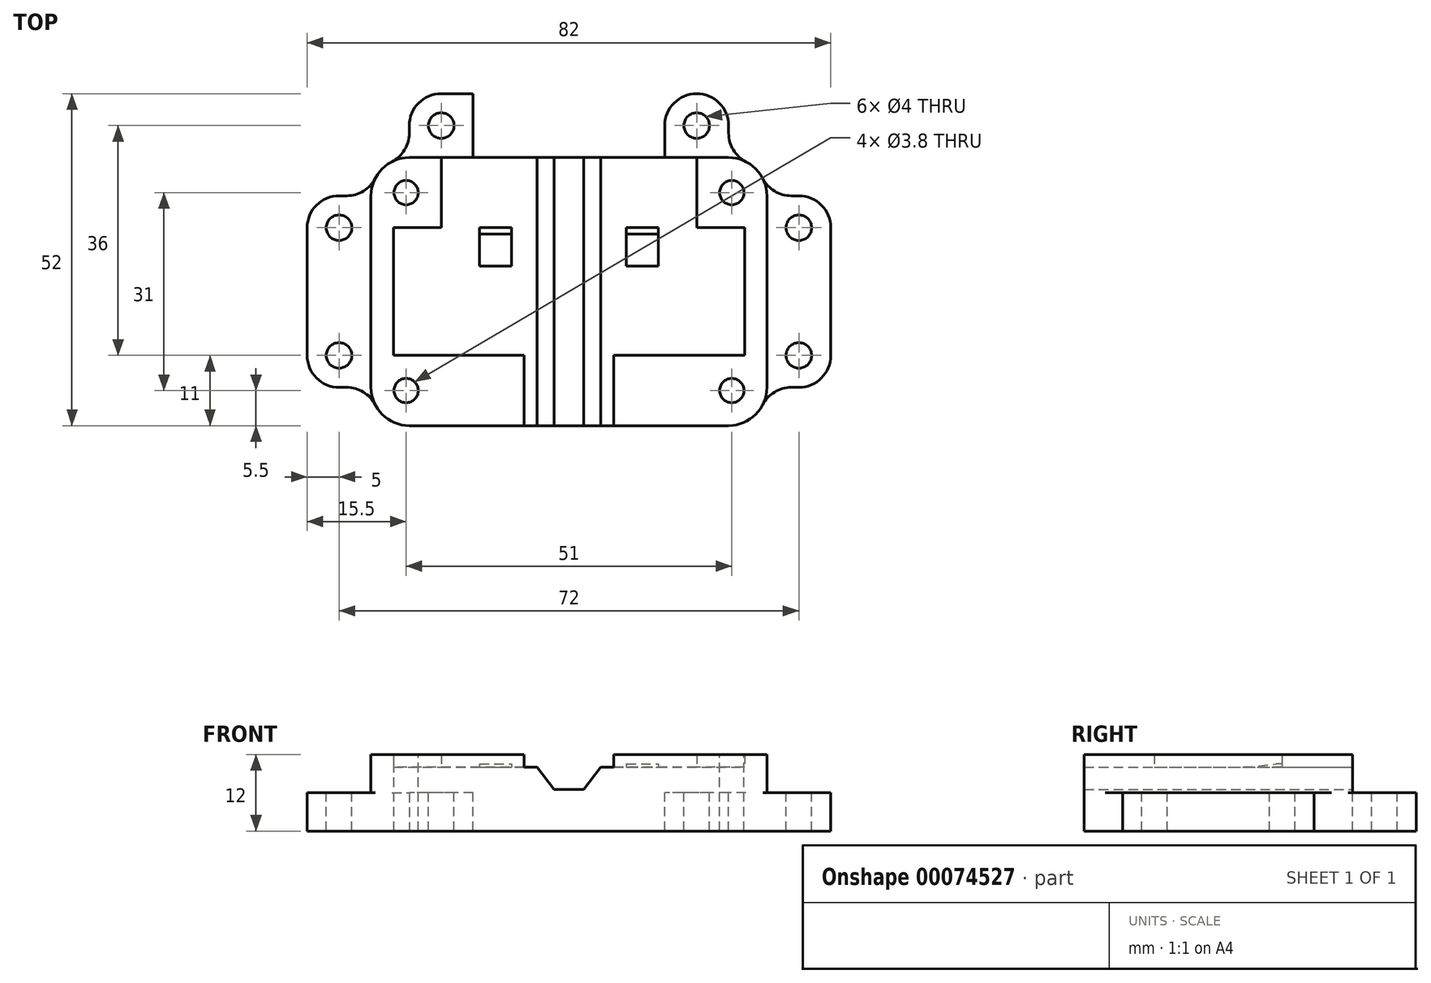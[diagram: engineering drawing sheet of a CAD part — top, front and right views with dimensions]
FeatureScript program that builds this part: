
annotation { "Feature Type Name" : "Feature", "Feature Type Description" : "" }
export const myFeature = defineFeature(function(context is Context, id is Id, definition is map)
    precondition{}
    {
        {
            var Q0;
            Q0=qCreatedBy(makeId("Front.planeOp"),FACE);
            var sketch = newSketch(context, id + "F0", { "sketchPlane" : qUnion([Q0])});
            skLineSegment(sketch, "E0.bottom", {"start": v(0, 0) * mm, "end": v(62, 0) * mm});
            skLineSegment(sketch, "E0.top", {"start": v(0, 10) * mm, "end": v(62, 10) * mm, "construction": true});
            skLineSegment(sketch, "E0.left", {"start": v(0, 0) * mm, "end": v(0, 10) * mm});
            skLineSegment(sketch, "E0.right", {"start": v(62, 0) * mm, "end": v(62, 10) * mm});
            skLineSegment(sketch, "E1", {"start": v(0, 10) * mm, "end": v(26, 10) * mm});
            skLineSegment(sketch, "E2", {"start": v(62, 10) * mm, "end": v(36, 10) * mm});
            skLineSegment(sketch, "E3", {"start": v(26, 10) * mm, "end": v(28.7, 6.5) * mm});
            skLineSegment(sketch, "E4", {"start": v(28.7, 6.5) * mm, "end": v(33.3, 6.5) * mm});
            skLineSegment(sketch, "E5", {"start": v(36, 10) * mm, "end": v(33.3, 6.5) * mm});
            skSolve(sketch);
        }
        {
            var Q0;
            Q0 = qSketchRegion(id + "F0", true);
            extrude(context, id + "F1", {"entities" : qUnion([Q0]), "depth" : 42 * mm});
        }
        {
            var Q0;
            Q0=makeQuery(id+"F1.opExtrude","SWEPT_FACE",FACE,{"disambiguationData":[OSD([sQuery(id+"F0.wireOp",EDGE,"E1")])]});
            var sketch = newSketch(context, id + "F2", { "sketchPlane" : qUnion([Q0])});
            skLineSegment(sketch, "E6", {"start": v(17, -8) * mm, "end": v(45, -8) * mm});
            skLineSegment(sketch, "E7", {"start": v(45, -8) * mm, "end": v(56.5, -27) * mm});
            skLineSegment(sketch, "E8", {"start": v(56.5, -27) * mm, "end": v(5.5, -27) * mm});
            skLineSegment(sketch, "E9", {"start": v(5.5, -27) * mm, "end": v(17, -8) * mm});
            skLineSegment(sketch, "E10.0", {"start": v(28.7, 0) * mm, "end": v(33.3, 0) * mm, "construction": true});
            skLineSegment(sketch, "E11", {"start": v(31, 0) * mm, "end": v(31, -8) * mm, "construction": true});
            skLineSegment(sketch, "E12", {"start": v(31, -8) * mm, "end": v(31, -27) * mm, "construction": true});
            skSolve(sketch);
        }
        {
            var Q0;
            {var subQ1=sQuery(id+"F2.wireOp",EDGE,"E9");Q0=makeQuery(id+"F2.imprint","IMPRINT",FACE,{"disambiguationData":[TD([[makeQuery(id+"F2.imprint","IMPRINT",EDGE,{"derivedFrom":subQ1}),1.0]])]});}
            var sketch = newSketch(context, id + "F3", { "sketchPlane" : qUnion([Q0])});
            skLineSegment(sketch, "E13.0", {"start": v(0, -42) * mm, "end": v(26, -42) * mm, "construction": true});
            skLineSegment(sketch, "E14.0", {"start": v(62, -42) * mm, "end": v(36, -42) * mm, "construction": true});
            skLineSegment(sketch, "E15", {"start": v(24, -42) * mm, "end": v(24, -31) * mm});
            skLineSegment(sketch, "E16", {"start": v(0, -42) * mm, "end": v(24, -42) * mm});
            skLineSegment(sketch, "E17", {"start": v(62, -42) * mm, "end": v(38, -42) * mm});
            skLineSegment(sketch, "E18", {"start": v(38, -42) * mm, "end": v(38, -31) * mm});
            skLineSegment(sketch, "E19", {"start": v(24, -31) * mm, "end": v(3.5, -31) * mm});
            skLineSegment(sketch, "E20", {"start": v(3.5, -31) * mm, "end": v(3.5, -11) * mm});
            skLineSegment(sketch, "E21", {"start": v(0, 0) * mm, "end": v(0, -42) * mm});
            skLineSegment(sketch, "E22", {"start": v(38, -31) * mm, "end": v(58.5, -31) * mm});
            skLineSegment(sketch, "E23", {"start": v(58.5, -31) * mm, "end": v(58.5, -11) * mm});
            skLineSegment(sketch, "E24", {"start": v(62, 0) * mm, "end": v(62, -42) * mm});
            skLineSegment(sketch, "E25", {"start": v(3.5, -11) * mm, "end": v(11, -11) * mm});
            skLineSegment(sketch, "E26", {"start": v(11, -11) * mm, "end": v(11, 0) * mm});
            skLineSegment(sketch, "E27", {"start": v(11, 0) * mm, "end": v(0, 0) * mm});
            skLineSegment(sketch, "E28", {"start": v(58.5, -11) * mm, "end": v(51, -11) * mm});
            skLineSegment(sketch, "E29", {"start": v(51, -11) * mm, "end": v(51, 0) * mm});
            skLineSegment(sketch, "E30", {"start": v(51, 0) * mm, "end": v(62, 0) * mm});
            skSolve(sketch);
        }
        {
            var Q0;
            Q0 = qSketchRegion(id + "F3", true);
            extrude(context, id + "F4", {"entities" : qUnion([Q0]), "operationType" : NewBodyOperationType.ADD, "depth" : 2 * mm});
        }
        {
            var Q0;
            Q0=makeQuery(id+"F4.opExtrude","CAP_FACE",FACE,{"disambiguationData":[OSD([sQuery(id+"F3.wireOp",EDGE,"E15"),sQuery(id+"F3.wireOp",EDGE,"E16"),sQuery(id+"F3.wireOp",EDGE,"E19"),sQuery(id+"F3.wireOp",EDGE,"E20"),sQuery(id+"F3.wireOp",EDGE,"E21"),sQuery(id+"F3.wireOp",EDGE,"E25"),sQuery(id+"F3.wireOp",EDGE,"E26"),sQuery(id+"F3.wireOp",EDGE,"E27")])],"isStart":false});
            var sketch = newSketch(context, id + "F5", { "sketchPlane" : qUnion([Q0])});
            skLineSegment(sketch, "E31.0", {"start": v(0, -42) * mm, "end": v(0, 0) * mm, "construction": true});
            skLineSegment(sketch, "E31.1", {"start": v(62, 0) * mm, "end": v(62, -42) * mm, "construction": true});
            skLineSegment(sketch, "E31.2", {"start": v(0, -42) * mm, "end": v(62, -42) * mm, "construction": true});
            skLineSegment(sketch, "E31.3", {"start": v(0, 0) * mm, "end": v(62, 0) * mm, "construction": true});
            skLineSegment(sketch, "E32", {"start": v(0, -36.5) * mm, "end": v(62, -36.5) * mm, "construction": true});
            skLineSegment(sketch, "E33", {"start": v(0, -5.5) * mm, "end": v(62, -5.5) * mm, "construction": true});
            skLineSegment(sketch, "E34", {"start": v(5.5, 0) * mm, "end": v(5.5, -42) * mm, "construction": true});
            skLineSegment(sketch, "E35", {"start": v(56.5, 0) * mm, "end": v(56.5, -42) * mm, "construction": true});
            skCircle(sketch, "E36", {"center": v(5.5, -5.5) * mm, "radius": 1.9 * mm});
            skCircle(sketch, "E37", {"center": v(56.5, -5.5) * mm, "radius": 1.9 * mm});
            skCircle(sketch, "E38", {"center": v(5.5, -36.5) * mm, "radius": 1.9 * mm});
            skCircle(sketch, "E39", {"center": v(56.5, -36.5) * mm, "radius": 1.9 * mm});
            skSolve(sketch);
        }
        {
            var Q0;
            Q0 = qSketchRegion(id + "F5", true);
            var Q1;
            Q1=makeQuery(id+"F1.opExtrude","SWEPT_FACE",FACE,{"disambiguationData":[OSD([sQuery(id+"F0.wireOp",EDGE,"E0.bottom")])]});
            extrude(context, id + "F6", {"entities" : qUnion([Q0]), "operationType" : NewBodyOperationType.REMOVE, "endBound" : BoundingType.UP_TO_SURFACE, "oppositeDirection" : true, "endBoundEntityFace" : qUnion([Q1]), "depth" : 25 * mm});
        }
        {
            var Q0;
            Q0=makeQuery(id+"F4.boolean.opBoolean","MERGE",EDGE,{"derivedFrom":[makeQuery(id+"F1.opExtrude","CAP_EDGE",EDGE,{"disambiguationData":[OSD([sQuery(id+"F0.wireOp",EDGE,"E0.left")])],"isStart":false}),makeQuery(id+"F4.opExtrude","SWEPT_EDGE",EDGE,{"disambiguationData":[OSD([sQuery(id+"F3.wireOp",EDGE,"E16"),sQuery(id+"F3.wireOp",EDGE,"E21")])]})]});
            var Q1;
            Q1=makeQuery(id+"F4.boolean.opBoolean","MERGE",EDGE,{"derivedFrom":[makeQuery(id+"F1.opExtrude","CAP_EDGE",EDGE,{"disambiguationData":[OSD([sQuery(id+"F0.wireOp",EDGE,"E0.left")])],"isStart":true}),makeQuery(id+"F4.opExtrude","SWEPT_EDGE",EDGE,{"disambiguationData":[OSD([sQuery(id+"F3.wireOp",EDGE,"E21"),sQuery(id+"F3.wireOp",EDGE,"E27")])]})]});
            var Q2;
            Q2=makeQuery(id+"F4.boolean.opBoolean","MERGE",EDGE,{"derivedFrom":[makeQuery(id+"F1.opExtrude","CAP_EDGE",EDGE,{"disambiguationData":[OSD([sQuery(id+"F0.wireOp",EDGE,"E0.right")])],"isStart":false}),makeQuery(id+"F4.opExtrude","SWEPT_EDGE",EDGE,{"disambiguationData":[OSD([sQuery(id+"F3.wireOp",EDGE,"E17"),sQuery(id+"F3.wireOp",EDGE,"E24")])]})]});
            var Q3;
            Q3=makeQuery(id+"F4.boolean.opBoolean","MERGE",EDGE,{"derivedFrom":[makeQuery(id+"F1.opExtrude","CAP_EDGE",EDGE,{"disambiguationData":[OSD([sQuery(id+"F0.wireOp",EDGE,"E0.right")])],"isStart":true}),makeQuery(id+"F4.opExtrude","SWEPT_EDGE",EDGE,{"disambiguationData":[OSD([sQuery(id+"F3.wireOp",EDGE,"E24"),sQuery(id+"F3.wireOp",EDGE,"E30")])]})]});
            fillet(context, id + "F7", {"entities" : qUnion([Q0, Q1, Q2, Q3]), "radius" : 6 * mm, "tangentPropagation" : true, "allowEdgeOverflow" : false});
        }
        {
            var Q0;
            Q0=makeQuery(id+"F4.boolean.opBoolean","MERGE",FACE,{"derivedFrom":[makeQuery(id+"F1.opExtrude","SWEPT_FACE",FACE,{"disambiguationData":[OSD([sQuery(id+"F0.wireOp",EDGE,"E0.right")])]}),makeQuery(id+"F4.opExtrude","SWEPT_FACE",FACE,{"disambiguationData":[OSD([sQuery(id+"F3.wireOp",EDGE,"E24")])]})]});
            var sketch = newSketch(context, id + "F8", { "sketchPlane" : qUnion([Q0])});
            skLineSegment(sketch, "E40.bottom", {"start": v(-6, 0) * mm, "end": v(-36, 0) * mm});
            skLineSegment(sketch, "E40.top", {"start": v(-6, 6) * mm, "end": v(-36, 6) * mm});
            skLineSegment(sketch, "E40.left", {"start": v(-6, 0) * mm, "end": v(-6, 6) * mm});
            skLineSegment(sketch, "E40.right", {"start": v(-36, 0) * mm, "end": v(-36, 6) * mm});
            skSolve(sketch);
        }
        {
            var Q0;
            Q0 = qSketchRegion(id + "F8", true);
            extrude(context, id + "F9", {"entities" : qUnion([Q0]), "operationType" : NewBodyOperationType.ADD, "depth" : 10 * mm});
        }
        {
            var Q0;
            Q0=makeQuery(id+"F4.boolean.opBoolean","MERGE",FACE,{"derivedFrom":[makeQuery(id+"F1.opExtrude","SWEPT_FACE",FACE,{"disambiguationData":[OSD([sQuery(id+"F0.wireOp",EDGE,"E0.left")])]}),makeQuery(id+"F4.opExtrude","SWEPT_FACE",FACE,{"disambiguationData":[OSD([sQuery(id+"F3.wireOp",EDGE,"E21")])]})]});
            var sketch = newSketch(context, id + "F10", { "sketchPlane" : qUnion([Q0])});
            skLineSegment(sketch, "E41.0", {"start": v(6, 6) * mm, "end": v(36, 6) * mm});
            skLineSegment(sketch, "E41.1", {"start": v(6, 0) * mm, "end": v(6, 6) * mm});
            skLineSegment(sketch, "E41.2", {"start": v(36, 0) * mm, "end": v(6, 0) * mm});
            skLineSegment(sketch, "E41.3", {"start": v(36, 6) * mm, "end": v(36, 0) * mm});
            skSolve(sketch);
        }
        {
            var Q0;
            Q0 = qSketchRegion(id + "F10", true);
            extrude(context, id + "F11", {"entities" : qUnion([Q0]), "operationType" : NewBodyOperationType.ADD, "depth" : 10 * mm});
        }
        {
            var Q0;
            Q0=makeQuery(id+"F4.boolean.opBoolean","MERGE",FACE,{"derivedFrom":[makeQuery(id+"F1.opExtrude","CAP_FACE",FACE,{"disambiguationData":[OSD([sQuery(id+"F0.wireOp",EDGE,"E0.bottom"),sQuery(id+"F0.wireOp",EDGE,"E0.left"),sQuery(id+"F0.wireOp",EDGE,"E0.right"),sQuery(id+"F0.wireOp",EDGE,"E1"),sQuery(id+"F0.wireOp",EDGE,"E2"),sQuery(id+"F0.wireOp",EDGE,"E3"),sQuery(id+"F0.wireOp",EDGE,"E4"),sQuery(id+"F0.wireOp",EDGE,"E5")])],"isStart":true}),makeQuery(id+"F4.opExtrude","SWEPT_FACE",FACE,{"disambiguationData":[OSD([sQuery(id+"F3.wireOp",EDGE,"E27")])]}),makeQuery(id+"F4.opExtrude","SWEPT_FACE",FACE,{"disambiguationData":[OSD([sQuery(id+"F3.wireOp",EDGE,"E30")])]})]});
            var sketch = newSketch(context, id + "F12", { "sketchPlane" : qUnion([Q0])});
            skLineSegment(sketch, "E42.bottom", {"start": v(-56, 0) * mm, "end": v(-6, 0) * mm});
            skLineSegment(sketch, "E42.top", {"start": v(-56, 6) * mm, "end": v(-6, 6) * mm});
            skLineSegment(sketch, "E42.left", {"start": v(-56, 0) * mm, "end": v(-56, 6) * mm});
            skLineSegment(sketch, "E42.right", {"start": v(-6, 0) * mm, "end": v(-6, 6) * mm});
            skSolve(sketch);
        }
        {
            var Q0;
            Q0 = qSketchRegion(id + "F12", true);
            extrude(context, id + "F13", {"entities" : qUnion([Q0]), "operationType" : NewBodyOperationType.ADD, "depth" : 10 * mm});
        }
        {
            var Q0;
            Q0=makeQuery(id+"F13.opExtrude","CAP_EDGE",EDGE,{"disambiguationData":[OSD([sQuery(id+"F12.wireOp",EDGE,"E42.right")])],"isStart":false});
            var Q1;
            Q1=makeQuery(id+"F11.opExtrude","CAP_EDGE",EDGE,{"disambiguationData":[OSD([sQuery(id+"F10.wireOp",EDGE,"E41.1")])],"isStart":false});
            var Q2;
            Q2=makeQuery(id+"F11.opExtrude","CAP_EDGE",EDGE,{"disambiguationData":[OSD([sQuery(id+"F10.wireOp",EDGE,"E41.3")])],"isStart":false});
            var Q3;
            Q3=makeQuery(id+"F13.opExtrude","CAP_EDGE",EDGE,{"disambiguationData":[OSD([sQuery(id+"F12.wireOp",EDGE,"E42.left")])],"isStart":false});
            var Q4;
            Q4=makeQuery(id+"F9.opExtrude","CAP_EDGE",EDGE,{"disambiguationData":[OSD([sQuery(id+"F8.wireOp",EDGE,"E40.left")])],"isStart":false});
            var Q5;
            Q5=makeQuery(id+"F9.opExtrude","CAP_EDGE",EDGE,{"disambiguationData":[OSD([sQuery(id+"F8.wireOp",EDGE,"E40.right")])],"isStart":false});
            var Q6;
            {var subQ0=sQuery(id+"F3.wireOp",EDGE,"E27");var subQ1=sQuery(id+"F0.wireOp",EDGE,"E0.left");Q6=makeQuery(id+"F13.boolean.opBoolean","MERGE",EDGE,{"derivedFrom":[makeQuery(id+"F7.opFillet","BLEND_EDGE",EDGE,{"blendedFrom":[makeQuery(id+"F4.boolean.opBoolean","MERGE",EDGE,{"derivedFrom":[makeQuery(id+"F1.opExtrude","CAP_EDGE",EDGE,{"disambiguationData":[OSD([subQ1])],"isStart":true}),makeQuery(id+"F4.opExtrude","SWEPT_EDGE",EDGE,{"disambiguationData":[OSD([sQuery(id+"F3.wireOp",EDGE,"E21"),subQ0])]})]}),makeQuery(id+"F4.boolean.opBoolean","MERGE",FACE,{"derivedFrom":[makeQuery(id+"F1.opExtrude","CAP_FACE",FACE,{"disambiguationData":[OSD([sQuery(id+"F0.wireOp",EDGE,"E0.bottom"),subQ1,sQuery(id+"F0.wireOp",EDGE,"E0.right"),sQuery(id+"F0.wireOp",EDGE,"E1"),sQuery(id+"F0.wireOp",EDGE,"E2"),sQuery(id+"F0.wireOp",EDGE,"E3"),sQuery(id+"F0.wireOp",EDGE,"E4"),sQuery(id+"F0.wireOp",EDGE,"E5")])],"isStart":true}),makeQuery(id+"F4.opExtrude","SWEPT_FACE",FACE,{"disambiguationData":[OSD([subQ0])]}),makeQuery(id+"F4.opExtrude","SWEPT_FACE",FACE,{"disambiguationData":[OSD([sQuery(id+"F3.wireOp",EDGE,"E30")])]})]})],"blendedInto":[makeQuery(id+"F4.boolean.opBoolean","MERGE",FACE,{"derivedFrom":[makeQuery(id+"F1.opExtrude","CAP_FACE",FACE,{"disambiguationData":[OSD([sQuery(id+"F0.wireOp",EDGE,"E0.bottom"),subQ1,sQuery(id+"F0.wireOp",EDGE,"E0.right"),sQuery(id+"F0.wireOp",EDGE,"E1"),sQuery(id+"F0.wireOp",EDGE,"E2"),sQuery(id+"F0.wireOp",EDGE,"E3"),sQuery(id+"F0.wireOp",EDGE,"E4"),sQuery(id+"F0.wireOp",EDGE,"E5")])],"isStart":true}),makeQuery(id+"F4.opExtrude","SWEPT_FACE",FACE,{"disambiguationData":[OSD([subQ0])]}),makeQuery(id+"F4.opExtrude","SWEPT_FACE",FACE,{"disambiguationData":[OSD([sQuery(id+"F3.wireOp",EDGE,"E30")])]})]})]}),makeQuery(id+"F13.opExtrude","CAP_EDGE",EDGE,{"disambiguationData":[OSD([sQuery(id+"F12.wireOp",EDGE,"E42.right")])],"isStart":true})]});}
            var Q7;
            {var subQ0=sQuery(id+"F3.wireOp",EDGE,"E21");var subQ1=sQuery(id+"F0.wireOp",EDGE,"E0.left");Q7=makeQuery(id+"F11.boolean.opBoolean","MERGE",EDGE,{"derivedFrom":[makeQuery(id+"F7.opFillet","BLEND_EDGE",EDGE,{"blendedFrom":[makeQuery(id+"F4.boolean.opBoolean","MERGE",EDGE,{"derivedFrom":[makeQuery(id+"F1.opExtrude","CAP_EDGE",EDGE,{"disambiguationData":[OSD([subQ1])],"isStart":true}),makeQuery(id+"F4.opExtrude","SWEPT_EDGE",EDGE,{"disambiguationData":[OSD([subQ0,sQuery(id+"F3.wireOp",EDGE,"E27")])]})]}),makeQuery(id+"F4.boolean.opBoolean","MERGE",FACE,{"derivedFrom":[makeQuery(id+"F1.opExtrude","SWEPT_FACE",FACE,{"disambiguationData":[OSD([subQ1])]}),makeQuery(id+"F4.opExtrude","SWEPT_FACE",FACE,{"disambiguationData":[OSD([subQ0])]})]})],"blendedInto":[makeQuery(id+"F4.boolean.opBoolean","MERGE",FACE,{"derivedFrom":[makeQuery(id+"F1.opExtrude","SWEPT_FACE",FACE,{"disambiguationData":[OSD([subQ1])]}),makeQuery(id+"F4.opExtrude","SWEPT_FACE",FACE,{"disambiguationData":[OSD([subQ0])]})]})]}),makeQuery(id+"F11.opExtrude","CAP_EDGE",EDGE,{"disambiguationData":[OSD([sQuery(id+"F10.wireOp",EDGE,"E41.1")])],"isStart":true})]});}
            var Q8;
            {var subQ0=sQuery(id+"F3.wireOp",EDGE,"E21");var subQ1=sQuery(id+"F0.wireOp",EDGE,"E0.left");Q8=makeQuery(id+"F11.boolean.opBoolean","MERGE",EDGE,{"derivedFrom":[makeQuery(id+"F7.opFillet","BLEND_EDGE",EDGE,{"blendedFrom":[makeQuery(id+"F4.boolean.opBoolean","MERGE",EDGE,{"derivedFrom":[makeQuery(id+"F1.opExtrude","CAP_EDGE",EDGE,{"disambiguationData":[OSD([subQ1])],"isStart":false}),makeQuery(id+"F4.opExtrude","SWEPT_EDGE",EDGE,{"disambiguationData":[OSD([sQuery(id+"F3.wireOp",EDGE,"E16"),subQ0])]})]}),makeQuery(id+"F4.boolean.opBoolean","MERGE",FACE,{"derivedFrom":[makeQuery(id+"F1.opExtrude","SWEPT_FACE",FACE,{"disambiguationData":[OSD([subQ1])]}),makeQuery(id+"F4.opExtrude","SWEPT_FACE",FACE,{"disambiguationData":[OSD([subQ0])]})]})],"blendedInto":[makeQuery(id+"F4.boolean.opBoolean","MERGE",FACE,{"derivedFrom":[makeQuery(id+"F1.opExtrude","SWEPT_FACE",FACE,{"disambiguationData":[OSD([subQ1])]}),makeQuery(id+"F4.opExtrude","SWEPT_FACE",FACE,{"disambiguationData":[OSD([subQ0])]})]})]}),makeQuery(id+"F11.opExtrude","CAP_EDGE",EDGE,{"disambiguationData":[OSD([sQuery(id+"F10.wireOp",EDGE,"E41.3")])],"isStart":true})]});}
            var Q9;
            {var subQ0=sQuery(id+"F3.wireOp",EDGE,"E30");var subQ1=sQuery(id+"F0.wireOp",EDGE,"E0.right");Q9=makeQuery(id+"F13.boolean.opBoolean","MERGE",EDGE,{"derivedFrom":[makeQuery(id+"F7.opFillet","BLEND_EDGE",EDGE,{"blendedFrom":[makeQuery(id+"F4.boolean.opBoolean","MERGE",EDGE,{"derivedFrom":[makeQuery(id+"F1.opExtrude","CAP_EDGE",EDGE,{"disambiguationData":[OSD([subQ1])],"isStart":true}),makeQuery(id+"F4.opExtrude","SWEPT_EDGE",EDGE,{"disambiguationData":[OSD([sQuery(id+"F3.wireOp",EDGE,"E24"),subQ0])]})]}),makeQuery(id+"F4.boolean.opBoolean","MERGE",FACE,{"derivedFrom":[makeQuery(id+"F1.opExtrude","CAP_FACE",FACE,{"disambiguationData":[OSD([sQuery(id+"F0.wireOp",EDGE,"E0.bottom"),sQuery(id+"F0.wireOp",EDGE,"E0.left"),subQ1,sQuery(id+"F0.wireOp",EDGE,"E1"),sQuery(id+"F0.wireOp",EDGE,"E2"),sQuery(id+"F0.wireOp",EDGE,"E3"),sQuery(id+"F0.wireOp",EDGE,"E4"),sQuery(id+"F0.wireOp",EDGE,"E5")])],"isStart":true}),makeQuery(id+"F4.opExtrude","SWEPT_FACE",FACE,{"disambiguationData":[OSD([sQuery(id+"F3.wireOp",EDGE,"E27")])]}),makeQuery(id+"F4.opExtrude","SWEPT_FACE",FACE,{"disambiguationData":[OSD([subQ0])]})]})],"blendedInto":[makeQuery(id+"F4.boolean.opBoolean","MERGE",FACE,{"derivedFrom":[makeQuery(id+"F1.opExtrude","CAP_FACE",FACE,{"disambiguationData":[OSD([sQuery(id+"F0.wireOp",EDGE,"E0.bottom"),sQuery(id+"F0.wireOp",EDGE,"E0.left"),subQ1,sQuery(id+"F0.wireOp",EDGE,"E1"),sQuery(id+"F0.wireOp",EDGE,"E2"),sQuery(id+"F0.wireOp",EDGE,"E3"),sQuery(id+"F0.wireOp",EDGE,"E4"),sQuery(id+"F0.wireOp",EDGE,"E5")])],"isStart":true}),makeQuery(id+"F4.opExtrude","SWEPT_FACE",FACE,{"disambiguationData":[OSD([sQuery(id+"F3.wireOp",EDGE,"E27")])]}),makeQuery(id+"F4.opExtrude","SWEPT_FACE",FACE,{"disambiguationData":[OSD([subQ0])]})]})]}),makeQuery(id+"F13.opExtrude","CAP_EDGE",EDGE,{"disambiguationData":[OSD([sQuery(id+"F12.wireOp",EDGE,"E42.left")])],"isStart":true})]});}
            var Q10;
            {var subQ0=sQuery(id+"F3.wireOp",EDGE,"E24");var subQ1=sQuery(id+"F0.wireOp",EDGE,"E0.right");Q10=makeQuery(id+"F9.boolean.opBoolean","MERGE",EDGE,{"derivedFrom":[makeQuery(id+"F7.opFillet","BLEND_EDGE",EDGE,{"blendedFrom":[makeQuery(id+"F4.boolean.opBoolean","MERGE",EDGE,{"derivedFrom":[makeQuery(id+"F1.opExtrude","CAP_EDGE",EDGE,{"disambiguationData":[OSD([subQ1])],"isStart":true}),makeQuery(id+"F4.opExtrude","SWEPT_EDGE",EDGE,{"disambiguationData":[OSD([subQ0,sQuery(id+"F3.wireOp",EDGE,"E30")])]})]}),makeQuery(id+"F4.boolean.opBoolean","MERGE",FACE,{"derivedFrom":[makeQuery(id+"F1.opExtrude","SWEPT_FACE",FACE,{"disambiguationData":[OSD([subQ1])]}),makeQuery(id+"F4.opExtrude","SWEPT_FACE",FACE,{"disambiguationData":[OSD([subQ0])]})]})],"blendedInto":[makeQuery(id+"F4.boolean.opBoolean","MERGE",FACE,{"derivedFrom":[makeQuery(id+"F1.opExtrude","SWEPT_FACE",FACE,{"disambiguationData":[OSD([subQ1])]}),makeQuery(id+"F4.opExtrude","SWEPT_FACE",FACE,{"disambiguationData":[OSD([subQ0])]})]})]}),makeQuery(id+"F9.opExtrude","CAP_EDGE",EDGE,{"disambiguationData":[OSD([sQuery(id+"F8.wireOp",EDGE,"E40.left")])],"isStart":true})]});}
            var Q11;
            {var subQ0=sQuery(id+"F3.wireOp",EDGE,"E24");var subQ1=sQuery(id+"F0.wireOp",EDGE,"E0.right");Q11=makeQuery(id+"F9.boolean.opBoolean","MERGE",EDGE,{"derivedFrom":[makeQuery(id+"F7.opFillet","BLEND_EDGE",EDGE,{"blendedFrom":[makeQuery(id+"F4.boolean.opBoolean","MERGE",EDGE,{"derivedFrom":[makeQuery(id+"F1.opExtrude","CAP_EDGE",EDGE,{"disambiguationData":[OSD([subQ1])],"isStart":false}),makeQuery(id+"F4.opExtrude","SWEPT_EDGE",EDGE,{"disambiguationData":[OSD([sQuery(id+"F3.wireOp",EDGE,"E17"),subQ0])]})]}),makeQuery(id+"F4.boolean.opBoolean","MERGE",FACE,{"derivedFrom":[makeQuery(id+"F1.opExtrude","SWEPT_FACE",FACE,{"disambiguationData":[OSD([subQ1])]}),makeQuery(id+"F4.opExtrude","SWEPT_FACE",FACE,{"disambiguationData":[OSD([subQ0])]})]})],"blendedInto":[makeQuery(id+"F4.boolean.opBoolean","MERGE",FACE,{"derivedFrom":[makeQuery(id+"F1.opExtrude","SWEPT_FACE",FACE,{"disambiguationData":[OSD([subQ1])]}),makeQuery(id+"F4.opExtrude","SWEPT_FACE",FACE,{"disambiguationData":[OSD([subQ0])]})]})]}),makeQuery(id+"F9.opExtrude","CAP_EDGE",EDGE,{"disambiguationData":[OSD([sQuery(id+"F8.wireOp",EDGE,"E40.right")])],"isStart":true})]});}
            fillet(context, id + "F14", {"entities" : qUnion([Q0, Q1, Q2, Q3, Q4, Q5, Q6, Q7, Q8, Q9, Q10, Q11]), "radius" : 5 * mm, "tangentPropagation" : true, "allowEdgeOverflow" : false});
        }
        {
            var Q0;
            Q0=makeQuery(id+"F11.opExtrude","SWEPT_FACE",FACE,{"disambiguationData":[OSD([sQuery(id+"F10.wireOp",EDGE,"E41.0")])]});
            var sketch = newSketch(context, id + "F15", { "sketchPlane" : qUnion([Q0])});
            skLineSegment(sketch, "E43", {"start": v(-5, -6) * mm, "end": v(-5, -36) * mm, "construction": true});
            skPoint(sketch, "E44.0", {"position": v(6, 5) * mm});
            skPoint(sketch, "E44.1", {"position": v(56, 5) * mm});
            skPoint(sketch, "E44.2", {"position": v(67, -6) * mm});
            skPoint(sketch, "E44.3", {"position": v(67, -36) * mm});
            skLineSegment(sketch, "E45", {"start": v(6, 5) * mm, "end": v(56, 5) * mm, "construction": true});
            skLineSegment(sketch, "E46", {"start": v(67, -6) * mm, "end": v(67, -36) * mm, "construction": true});
            skCircle(sketch, "E47", {"center": v(-5, -11) * mm, "radius": 2 * mm});
            skCircle(sketch, "E48", {"center": v(-5, -31) * mm, "radius": 2 * mm});
            skCircle(sketch, "E49", {"center": v(11, 5) * mm, "radius": 2 * mm});
            skCircle(sketch, "E50", {"center": v(51, 5) * mm, "radius": 2 * mm});
            skCircle(sketch, "E51", {"center": v(67, -11) * mm, "radius": 2 * mm});
            skCircle(sketch, "E52", {"center": v(67, -31) * mm, "radius": 2 * mm});
            skSolve(sketch);
        }
        {
            var Q0;
            Q0 = qSketchRegion(id + "F15", true);
            var Q1;
            Q1=makeQuery(id+"F13.boolean.opBoolean","MERGE",FACE,{"derivedFrom":[makeQuery(id+"F11.boolean.opBoolean","MERGE",FACE,{"derivedFrom":[makeQuery(id+"F9.boolean.opBoolean","MERGE",FACE,{"derivedFrom":[makeQuery(id+"F1.opExtrude","SWEPT_FACE",FACE,{"disambiguationData":[OSD([sQuery(id+"F0.wireOp",EDGE,"E0.bottom")])]}),makeQuery(id+"F9.opExtrude","SWEPT_FACE",FACE,{"disambiguationData":[OSD([sQuery(id+"F8.wireOp",EDGE,"E40.bottom")])]})]}),makeQuery(id+"F11.opExtrude","SWEPT_FACE",FACE,{"disambiguationData":[OSD([sQuery(id+"F10.wireOp",EDGE,"E41.2")])]})]}),makeQuery(id+"F13.opExtrude","SWEPT_FACE",FACE,{"disambiguationData":[OSD([sQuery(id+"F12.wireOp",EDGE,"E42.bottom")])]})]});
            extrude(context, id + "F16", {"entities" : qUnion([Q0]), "operationType" : NewBodyOperationType.REMOVE, "endBound" : BoundingType.UP_TO_SURFACE, "oppositeDirection" : true, "endBoundEntityFace" : qUnion([Q1]), "depth" : 25 * mm});
        }
        {
            var Q0;
            {var subQ0=sQuery(id+"F2.wireOp",EDGE,"E9");Q0=makeQuery(id+"F2.imprint","IMPRINT",FACE,{"disambiguationData":[TD([[makeQuery(id+"F2.imprint","IMPRINT",EDGE,{"derivedFrom":subQ0}),-1.0]])]});}
            var sketch = newSketch(context, id + "F17", { "sketchPlane" : qUnion([Q0])});
            skLineSegment(sketch, "E53.bottom", {"start": v(17, -11) * mm, "end": v(22, -11) * mm});
            skLineSegment(sketch, "E53.top", {"start": v(17, -17) * mm, "end": v(22, -17) * mm});
            skLineSegment(sketch, "E53.left", {"start": v(17, -11) * mm, "end": v(17, -17) * mm});
            skLineSegment(sketch, "E53.right", {"start": v(22, -11) * mm, "end": v(22, -17) * mm});
            skLineSegment(sketch, "E54.bottom", {"start": v(40, -11) * mm, "end": v(45, -11) * mm});
            skLineSegment(sketch, "E54.top", {"start": v(40, -17) * mm, "end": v(45, -17) * mm});
            skLineSegment(sketch, "E54.left", {"start": v(40, -11) * mm, "end": v(40, -17) * mm});
            skLineSegment(sketch, "E54.right", {"start": v(45, -11) * mm, "end": v(45, -17) * mm});
            skSolve(sketch);
        }
        {
            var Q0;
            Q0 = qSketchRegion(id + "F17", true);
            extrude(context, id + "F18", {"entities" : qUnion([Q0]), "operationType" : NewBodyOperationType.ADD, "depth" : 0.5 * mm});
        }
        {
            var Q0;
            Q0=makeQuery(id+"F18.opExtrude","CAP_EDGE",EDGE,{"disambiguationData":[OSD([sQuery(id+"F17.wireOp",EDGE,"E53.top")])],"isStart":false});
            var Q1;
            Q1=makeQuery(id+"F18.opExtrude","CAP_EDGE",EDGE,{"disambiguationData":[OSD([sQuery(id+"F17.wireOp",EDGE,"E54.top")])],"isStart":false});
            chamfer(context, id + "F19", {"entities" : qUnion([Q0, Q1]), "chamferType" : ChamferType.TWO_OFFSETS, "width1" : 5 * mm, "oppositeDirection" : false, "width2" : 0.5 * mm, "tangentPropagation" : true});
        }
        {
            var Q0;
            Q0=makeQuery(id+"F13.opExtrude","SWEPT_FACE",FACE,{"disambiguationData":[OSD([sQuery(id+"F12.wireOp",EDGE,"E42.top")])]});
            var sketch = newSketch(context, id + "F20", { "sketchPlane" : qUnion([Q0])});
            skLineSegment(sketch, "E55.bottom", {"start": v(16, 0) * mm, "end": v(46, 0) * mm});
            skLineSegment(sketch, "E55.top", {"start": v(16, 10) * mm, "end": v(46, 10) * mm});
            skLineSegment(sketch, "E55.left", {"start": v(16, 0) * mm, "end": v(16, 10) * mm});
            skLineSegment(sketch, "E55.right", {"start": v(46, 0) * mm, "end": v(46, 10) * mm});
            skSolve(sketch);
        }
        {
            var Q0;
            Q0 = qSketchRegion(id + "F20", true);
            var Q1;
            Q1=makeQuery(id+"F13.boolean.opBoolean","MERGE",FACE,{"derivedFrom":[makeQuery(id+"F11.boolean.opBoolean","MERGE",FACE,{"derivedFrom":[makeQuery(id+"F9.boolean.opBoolean","MERGE",FACE,{"derivedFrom":[makeQuery(id+"F1.opExtrude","SWEPT_FACE",FACE,{"disambiguationData":[OSD([sQuery(id+"F0.wireOp",EDGE,"E0.bottom")])]}),makeQuery(id+"F9.opExtrude","SWEPT_FACE",FACE,{"disambiguationData":[OSD([sQuery(id+"F8.wireOp",EDGE,"E40.bottom")])]})]}),makeQuery(id+"F11.opExtrude","SWEPT_FACE",FACE,{"disambiguationData":[OSD([sQuery(id+"F10.wireOp",EDGE,"E41.2")])]})]}),makeQuery(id+"F13.opExtrude","SWEPT_FACE",FACE,{"disambiguationData":[OSD([sQuery(id+"F12.wireOp",EDGE,"E42.bottom")])]})]});
            extrude(context, id + "F21", {"entities" : qUnion([Q0]), "operationType" : NewBodyOperationType.REMOVE, "endBound" : BoundingType.UP_TO_SURFACE, "oppositeDirection" : true, "endBoundEntityFace" : qUnion([Q1]), "depth" : 25 * mm});
        }
        {
            var Q0;
            Q0=makeQuery(id+"F21.boolean.opBoolean","COPY",EDGE,{"derivedFrom":makeQuery(id+"F21.opExtrude","SWEPT_EDGE",EDGE,{"disambiguationData":[OSD([sQuery(id+"F12.wireOp",EDGE,"E42.top"),sQuery(id+"F20.wireOp",EDGE,"E55.top"),sQuery(id+"F20.wireOp",EDGE,"E55.left")])]})});
            var Q1;
            Q1=makeQuery(id+"F21.boolean.opBoolean","COPY",EDGE,{"derivedFrom":makeQuery(id+"F21.opExtrude","SWEPT_EDGE",EDGE,{"disambiguationData":[OSD([sQuery(id+"F12.wireOp",EDGE,"E42.top"),sQuery(id+"F20.wireOp",EDGE,"E55.top"),sQuery(id+"F20.wireOp",EDGE,"E55.right")])]})});
            var Q2;
            Q2=makeQuery(id+"F21.boolean.opBoolean","COPY",EDGE,{"derivedFrom":makeQuery(id+"F21.opExtrude","SWEPT_EDGE",EDGE,{"disambiguationData":[OSD([sQuery(id+"F12.wireOp",EDGE,"E42.top"),sQuery(id+"F20.wireOp",EDGE,"E55.bottom"),sQuery(id+"F20.wireOp",EDGE,"E55.left")])]})});
            var Q3;
            Q3=makeQuery(id+"F21.boolean.opBoolean","COPY",EDGE,{"derivedFrom":makeQuery(id+"F21.opExtrude","SWEPT_EDGE",EDGE,{"disambiguationData":[OSD([sQuery(id+"F12.wireOp",EDGE,"E42.top"),sQuery(id+"F20.wireOp",EDGE,"E55.bottom"),sQuery(id+"F20.wireOp",EDGE,"E55.right")])]})});
            fillet(context, id + "F22", {"entities" : qUnion([Q0, Q1, Q2, Q3]), "radius" : 5 * mm, "tangentPropagation" : true, "allowEdgeOverflow" : false});
        }
    });
